# Revit family: KLA12 & AF12 - Freespace
name_source: partatom
category: Communication Devices
revit_build: Autodesk Revit 2017 (Build: 20190508_0315(x64)
units: mm (PartAtom-declared; Revit-internal decimal feet)

## family parameters
Always vertical = No
Cut with Voids When Loaded = No
Maintain Annotation Orientation = No
Part Type = Normal
Room Calculation Point = No
Round Connector Dimension = Use Diameter
Shared = No
Work Plane-Based = Yes

## types (3) — shared parameters
Coverage Horizontal = 90.00°
Coverage Vertical = 18.00°
Depth = 422 mm  [stored 1.38451 ft]
Description = 2-Way Line Array Element
Height = 381 mm  [stored 1.25 ft]
Manufacturer = QSC
Manufacturer URL = www.qsc.com
Model = KLA12
Product Documentation Link = https://www.qsc.com
Product Page URL = https://www.qsc.com
SPL Max = 131
Voltage AC = 100-240VAC, 50-60Hz
Weight Product (kg) = 25
Weight Product (lb) = 55
Width = 594 mm  [stored 1.94882 ft]
zero-valued in all types: Default Elevation

## per-type parameters (varying)
| type | AF12 Orientation | Show AF12 |
| KLA12 | QSC AF12 : Position A | No |
| KLA12 w/ AF12 Up Tilt | QSC AF12 : Position B | Yes |
| KLA12 w/ AF12 Down Tilt | QSC AF12 : Position A | Yes |

note: [stored X ft] marks values corroborated as IEEE doubles in the binary element streams (Revit-internal decimal feet)

## geometry (parser evidence)
native form markers: Blend x4, Sweep x18
no freeform markers — native parametric forms only
